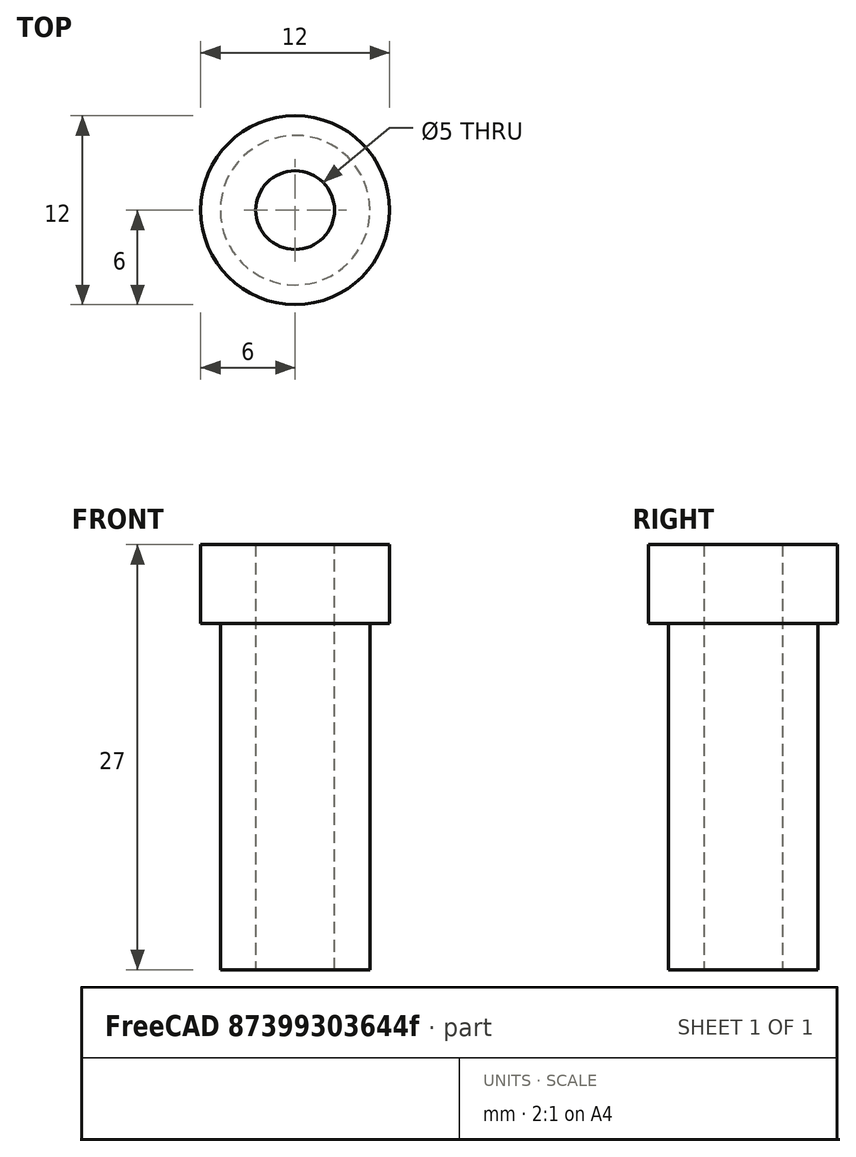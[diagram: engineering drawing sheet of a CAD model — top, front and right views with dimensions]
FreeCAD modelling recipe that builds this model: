
FCSTD DOCUMENT  (FreeCAD 0.18R4 (GitTag))
Label: keyboardSWPart2
License: All rights reserved
LicenseURL: http://en.wikipedia.org/wiki/All_rights_reserved
objects: Mesh::Feature×4, Sketcher::SketchObject×3, PartDesign::Pad×2, PartDesign::Pocket×1, PartDesign::Body×1
note: 10 computed .brp shape members not serialized (recipe doc carries the construction recipe); baked Part::Feature solids carry a one-line shape summary decoded from their .brp

FEATURE [Sketcher::SketchObject] Sketch
  MapMode = 5
  Support = -> [XY_Plane]
  sketch-geometry (1):
    g0: Circle CenterX=0 CenterY=0 CenterZ=0 NormalX=0 NormalY=0 NormalZ=1 AngleXU=0 Radius=6
  constraints (2):
    c: Coincident(g0,g-1)
    c: Radius(g0) = 6
FEATURE [PartDesign::Pad] Pad
  Length = 5
  Length2 = 100
  Profile = -> Sketch
  Type = 0
FEATURE [Sketcher::SketchObject] Sketch001
  MapMode = 5
  Placement = pos=(0,0,0) rot=(1,0,0;3.14159rad)
  Support = -> [Pad]
  sketch-geometry (1):
    g0: Circle CenterX=0 CenterY=0 CenterZ=0 NormalX=0 NormalY=0 NormalZ=1 AngleXU=0 Radius=4.75
  constraints (2):
    c: Coincident(g0,g-1)
    c: Radius(g0) = 4.75
FEATURE [PartDesign::Pad] Pad001
  BaseFeature = -> Pad
  Length = 22
  Length2 = 100
  Profile = -> Sketch001
  Type = 0
FEATURE [Sketcher::SketchObject] Sketch002
  MapMode = 5
  Placement = pos=(0,0,-22) rot=(1,0,0;3.14159rad)
  Support = -> [Pad001]
  sketch-geometry (1):
    g0: Circle CenterX=0 CenterY=0 CenterZ=0 NormalX=0 NormalY=0 NormalZ=1 AngleXU=0 Radius=2.5
  constraints (2):
    c: Coincident(g0,g-1)
    c: Radius(g0) = 2.5
FEATURE [PartDesign::Pocket] Pocket
  BaseFeature = -> Pad001
  Length = 30
  Length2 = 100
  Profile = -> Sketch002
  Type = 0
FEATURE [PartDesign::Body] Body
  Group = -> [Sketch,Pad,Sketch001,Pad001,Sketch002,Pocket]
  Origin = -> Origin
  Tip = -> Pocket
FEATURE [Mesh::Feature] Mesh  label="Body (Meshed)"
FEATURE [Mesh::Feature] Mesh001  label="Pad (Meshed)"
FEATURE [Mesh::Feature] Mesh002  label="Pad001 (Meshed)"
FEATURE [Mesh::Feature] Mesh003  label="Pocket (Meshed)"
